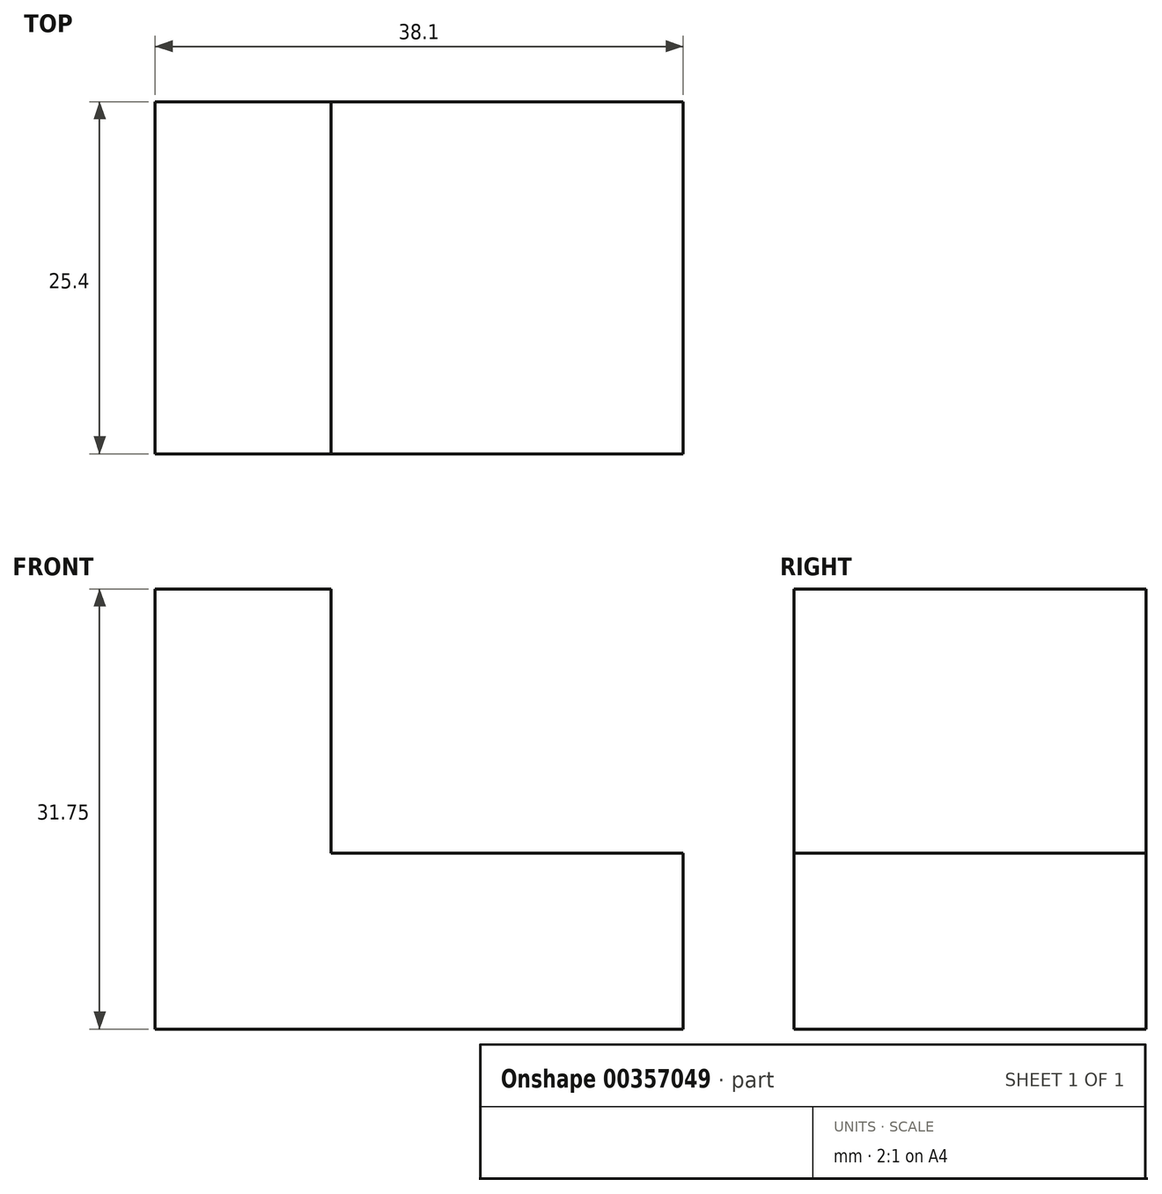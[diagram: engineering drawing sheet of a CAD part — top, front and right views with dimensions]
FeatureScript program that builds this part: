
annotation { "Feature Type Name" : "Feature", "Feature Type Description" : "" }
export const myFeature = defineFeature(function(context is Context, id is Id, definition is map)
    precondition{}
    {
        {
            var Q0;
            Q0=qCreatedBy(makeId("Front.planeOp"),FACE);
            var sketch = newSketch(context, id + "F0", { "sketchPlane" : qUnion([Q0])});
            skLineSegment(sketch, "E0", {"start": v(0, 0) * mm, "end": v(38.1, 0) * mm});
            skLineSegment(sketch, "E1", {"start": v(39.88, 0) * mm, "end": v(38.1, 0) * mm});
            skLineSegment(sketch, "E2", {"start": v(38.1, 0) * mm, "end": v(38.1, 12.7) * mm});
            skLineSegment(sketch, "E3", {"start": v(38.1, 12.7) * mm, "end": v(12.7, 12.7) * mm});
            skLineSegment(sketch, "E4", {"start": v(12.7, 12.7) * mm, "end": v(12.7, 31.75) * mm});
            skLineSegment(sketch, "E5", {"start": v(12.7, 31.75) * mm, "end": v(0, 31.75) * mm});
            skLineSegment(sketch, "E6", {"start": v(0, 31.75) * mm, "end": v(0, 0) * mm});
            skSolve(sketch);
        }
        {
            var Q0;
            Q0 = qSketchRegion(id + "F0", true);
            extrude(context, id + "F1", {"entities" : qUnion([Q0]), "oppositeDirection" : true, "depth" : 25.4 * mm});
        }
    });
